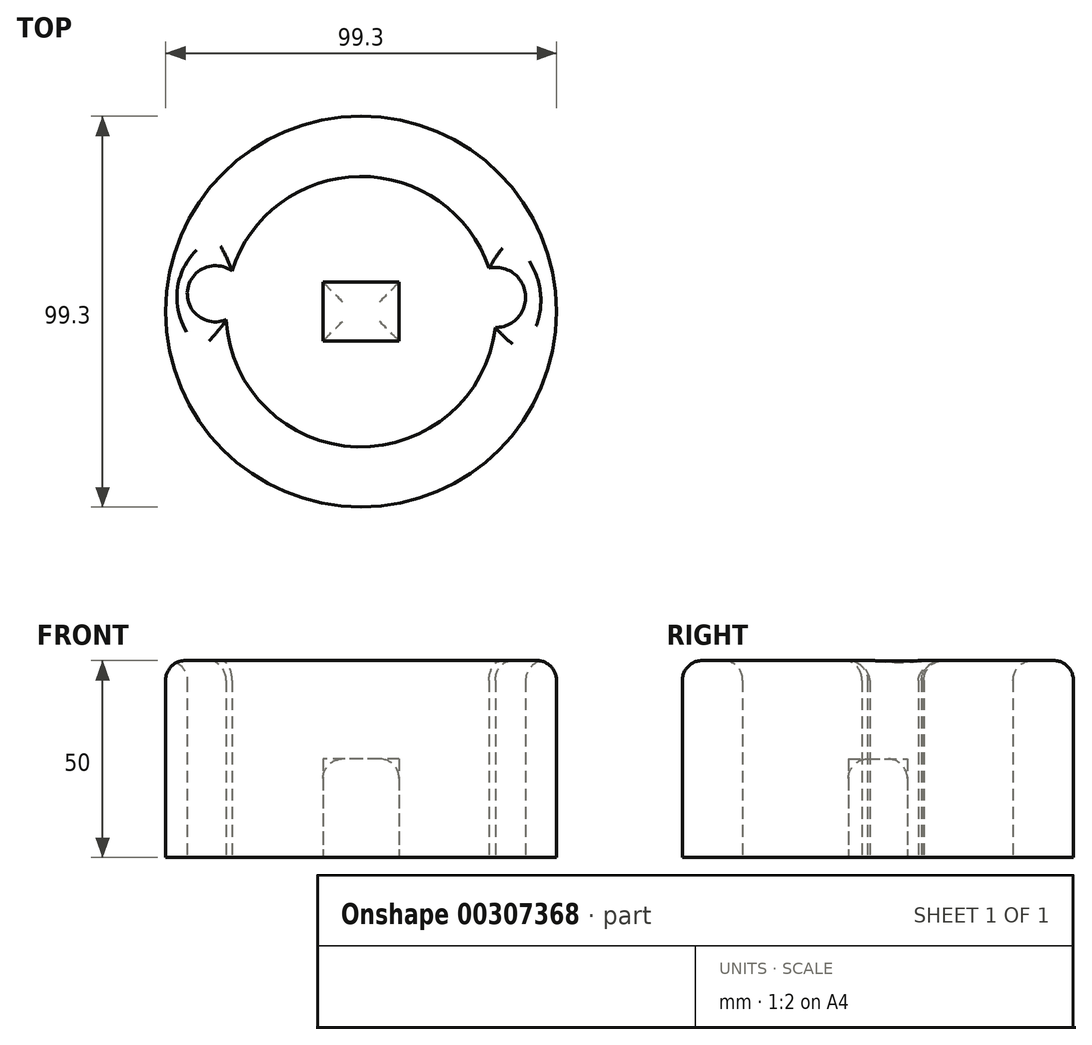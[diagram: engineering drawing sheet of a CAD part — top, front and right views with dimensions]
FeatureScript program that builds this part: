
annotation { "Feature Type Name" : "Feature", "Feature Type Description" : "" }
export const myFeature = defineFeature(function(context is Context, id is Id, definition is map)
    precondition{}
    {
        {
            var Q0;
            Q0=qCreatedBy(makeId("Top.planeOp"),FACE);
            var sketch = newSketch(context, id + "F0", { "sketchPlane" : qUnion([Q0])});
            skArc(sketch, "E0", {"start": v(-34.3, -2.07) * mm, "mid": v(-0.99, -34.34) * mm, "end": v(34.12, -4.04) * mm});
            skCircle(sketch, "E1", {"center": v(0, 0) * mm, "radius": 15 * mm});
            skCircle(sketch, "E2", {"center": v(0, 0) * mm, "radius": 26.25 * mm});
            skCircle(sketch, "E3", {"center": v(0, 0) * mm, "radius": 49.65 * mm});
            skLineSegment(sketch, "E4", {"start": v(-27.4, 20.73) * mm, "end": v(39.45, -30.14) * mm});
            skLineSegment(sketch, "E5", {"start": v(-27.4, 20.73) * mm, "end": v(-39.57, 29.99) * mm});
            skArc(sketch, "E6", {"start": v(34.12, -4.04) * mm, "mid": v(41.77, 4.4) * mm, "end": v(32.52, 11.07) * mm});
            skArc(sketch, "E7", {"start": v(-32.78, 10.29) * mm, "mid": v(-44.1, 5.4) * mm, "end": v(-34.3, -2.07) * mm});
            skArc(sketch, "E8.trimOffspring", {"start": v(32.52, 11.07) * mm, "mid": v(-0.41, 34.35) * mm, "end": v(-32.78, 10.29) * mm});
            skLineSegment(sketch, "E9", {"start": v(0, -15) * mm, "end": v(0, -34.34) * mm, "construction": true});
            skPoint(sketch, "E9.endSnap0", {"position": v(-0.99, -34.34) * mm});
            skLineSegment(sketch, "E10", {"start": v(0, -15) * mm, "end": v(0, -4.24) * mm, "construction": true});
            skLineSegment(sketch, "E11.bottom", {"start": v(9.69, -7.5) * mm, "end": v(-9.69, -7.5) * mm});
            skLineSegment(sketch, "E11.top", {"start": v(9.69, 7.5) * mm, "end": v(-9.69, 7.5) * mm});
            skLineSegment(sketch, "E11.left", {"start": v(9.69, -7.5) * mm, "end": v(9.69, 7.5) * mm});
            skLineSegment(sketch, "E11.right", {"start": v(-9.69, -7.5) * mm, "end": v(-9.69, 7.5) * mm});
            skSolve(sketch);
        }
        {
            var Q0;
            {var subQ5=sQuery(id+"F0.wireOp",EDGE,"E5");Q0=makeQuery(id+"F0.imprint","IMPRINT",FACE,{"disambiguationData":[TD([[makeQuery(id+"F0.imprint","IMPRINT",EDGE,{"derivedFrom":subQ5}),-1.0]])]});}
            var Q1;
            {var subQ0=sQuery(id+"F0.wireOp",EDGE,"E5");Q1=makeQuery(id+"F0.imprint","IMPRINT",FACE,{"disambiguationData":[TD([[makeQuery(id+"F0.imprint","IMPRINT",EDGE,{"derivedFrom":subQ0}),1.0]])]});}
            extrude(context, id + "F1", {"entities" : qUnion([Q0, Q1]), "depth" : 25 * mm});
        }
        {
            var Q0;
            {var subQ4=sQuery(id+"F0.wireOp",EDGE,"E11.top");Q0=makeQuery(id+"F0.imprint","IMPRINT",FACE,{"disambiguationData":[TD([[makeQuery(id+"F0.imprint","IMPRINT",EDGE,{"derivedFrom":subQ4}),1.0]])]});}
            var Q1;
            {var subQ0=sQuery(id+"F0.wireOp",EDGE,"E11.bottom");Q1=makeQuery(id+"F0.imprint","IMPRINT",FACE,{"disambiguationData":[TD([[makeQuery(id+"F0.imprint","IMPRINT",EDGE,{"derivedFrom":subQ0}),-1.0]])]});}
            var Q2;
            Q2=makeQuery(id+"F1.opExtrude","CAP_FACE",FACE,{"disambiguationData":[OSD([sQuery(id+"F0.wireOp",EDGE,"E0"),sQuery(id+"F0.wireOp",EDGE,"E3"),sQuery(id+"F0.wireOp",EDGE,"E6"),sQuery(id+"F0.wireOp",EDGE,"E7"),sQuery(id+"F0.wireOp",EDGE,"E8.trimOffspring")])],"isStart":false});
            extrude(context, id + "F2", {"entities" : qUnion([Q0, Q1, Q2]), "depth" : 25 * mm});
        }
        {
            var Q0;
            {var subQ0=sQuery(id+"F0.wireOp",EDGE,"E5");Q0=makeQuery(id+"F0.imprint","IMPRINT",FACE,{"disambiguationData":[TD([[makeQuery(id+"F0.imprint","IMPRINT",EDGE,{"derivedFrom":subQ0}),1.0]])]});}
            var Q1;
            {var subQ4=sQuery(id+"F0.wireOp",EDGE,"E11.top");Q1=makeQuery(id+"F0.imprint","IMPRINT",FACE,{"disambiguationData":[TD([[makeQuery(id+"F0.imprint","IMPRINT",EDGE,{"derivedFrom":subQ4}),1.0]])]});}
            var Q2;
            {var subQ0=sQuery(id+"F0.wireOp",EDGE,"E11.bottom");Q2=makeQuery(id+"F0.imprint","IMPRINT",FACE,{"disambiguationData":[TD([[makeQuery(id+"F0.imprint","IMPRINT",EDGE,{"derivedFrom":subQ0}),-1.0]])]});}
            extrude(context, id + "F3", {"entities" : qUnion([Q0, Q1, Q2]), "depth" : 25 * mm});
        }
        {
            var Q0;
            {var subQ5=sQuery(id+"F0.wireOp",EDGE,"E5");Q0=makeQuery(id+"F0.imprint","IMPRINT",FACE,{"disambiguationData":[TD([[makeQuery(id+"F0.imprint","IMPRINT",EDGE,{"derivedFrom":subQ5}),-1.0]])]});}
            extrude(context, id + "F4", {"entities" : qUnion([Q0]), "operationType" : NewBodyOperationType.ADD, "depth" : 30 * mm});
        }
        {
            var Q0;
            Q0=makeQuery(id+"F2.opExtrude","CAP_EDGE",EDGE,{"disambiguationData":[OSD([sQuery(id+"F0.wireOp",EDGE,"E3")])],"isStart":false});
            var Q1;
            Q1=makeQuery(id+"F2.opExtrude","CAP_EDGE",EDGE,{"disambiguationData":[OSD([sQuery(id+"F0.wireOp",EDGE,"E8.trimOffspring")])],"isStart":false});
            var Q2;
            Q2=makeQuery(id+"F2.opExtrude","CAP_EDGE",EDGE,{"disambiguationData":[OSD([sQuery(id+"F0.wireOp",EDGE,"E7")])],"isStart":false});
            var Q3;
            Q3=makeQuery(id+"F2.opExtrude","CAP_EDGE",EDGE,{"disambiguationData":[OSD([sQuery(id+"F0.wireOp",EDGE,"E0")])],"isStart":false});
            var Q4;
            Q4=makeQuery(id+"F2.opExtrude","CAP_EDGE",EDGE,{"disambiguationData":[OSD([sQuery(id+"F0.wireOp",EDGE,"E6")])],"isStart":false});
            fillet(context, id + "F5", {"entities" : qUnion([Q0, Q1, Q2, Q3, Q4]), "radius" : 5 * mm, "tangentPropagation" : true, "allowEdgeOverflow" : false});
        }
        {
            var Q0;
            Q0=makeQuery(id+"F2.opExtrude","CAP_FACE",FACE,{"disambiguationData":[OSD([sQuery(id+"F0.wireOp",EDGE,"E11.bottom"),sQuery(id+"F0.wireOp",EDGE,"E11.top"),sQuery(id+"F0.wireOp",EDGE,"E11.left"),sQuery(id+"F0.wireOp",EDGE,"E11.right")])],"isStart":false});
            var Q1;
            Q1=makeQuery(id+"F2.opExtrude","CAP_EDGE",EDGE,{"disambiguationData":[OSD([sQuery(id+"F0.wireOp",EDGE,"E11.right")])],"isStart":false});
            var Q2;
            Q2=makeQuery(id+"F2.opExtrude","CAP_EDGE",EDGE,{"disambiguationData":[OSD([sQuery(id+"F0.wireOp",EDGE,"E11.bottom")])],"isStart":false});
            var Q3;
            Q3=makeQuery(id+"F2.opExtrude","CAP_EDGE",EDGE,{"disambiguationData":[OSD([sQuery(id+"F0.wireOp",EDGE,"E11.left")])],"isStart":false});
            fillet(context, id + "F6", {"entities" : qUnion([Q0, Q1, Q2, Q3]), "radius" : 5 * mm, "tangentPropagation" : true, "allowEdgeOverflow" : false});
        }
    });
